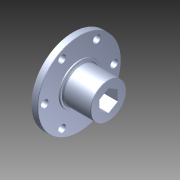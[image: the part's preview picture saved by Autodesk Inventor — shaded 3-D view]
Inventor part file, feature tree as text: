
AUTODESK INVENTOR PART (.ipt)
format: ipt  version: 2015 (Build 190159000, 159)  size: 155,648 bytes
history: native  units: in
note: dims shown in document units (in); Inventor stores cm internally (conversion verified against a paired STEP export)
features: chamfer x1, other x1, imported_body x1
ambient origin geometry x8: Origin, YZ Plane, XZ Plane, XY Plane, X Axis, Y Axis, Z Axis, Center Point
bodies: Body1 (feature_tree)
feature tree (3):
  chamfer  "Chamfer3"  [1 undecoded]
  other  "hub hex 0.5in1"
  imported_body  "Base1"
note: 1 required parameter value undecoded (feature->parameter linkage not recoverable at this tier; creation-order binding heuristic only, values carry confidence <= 0.55)
